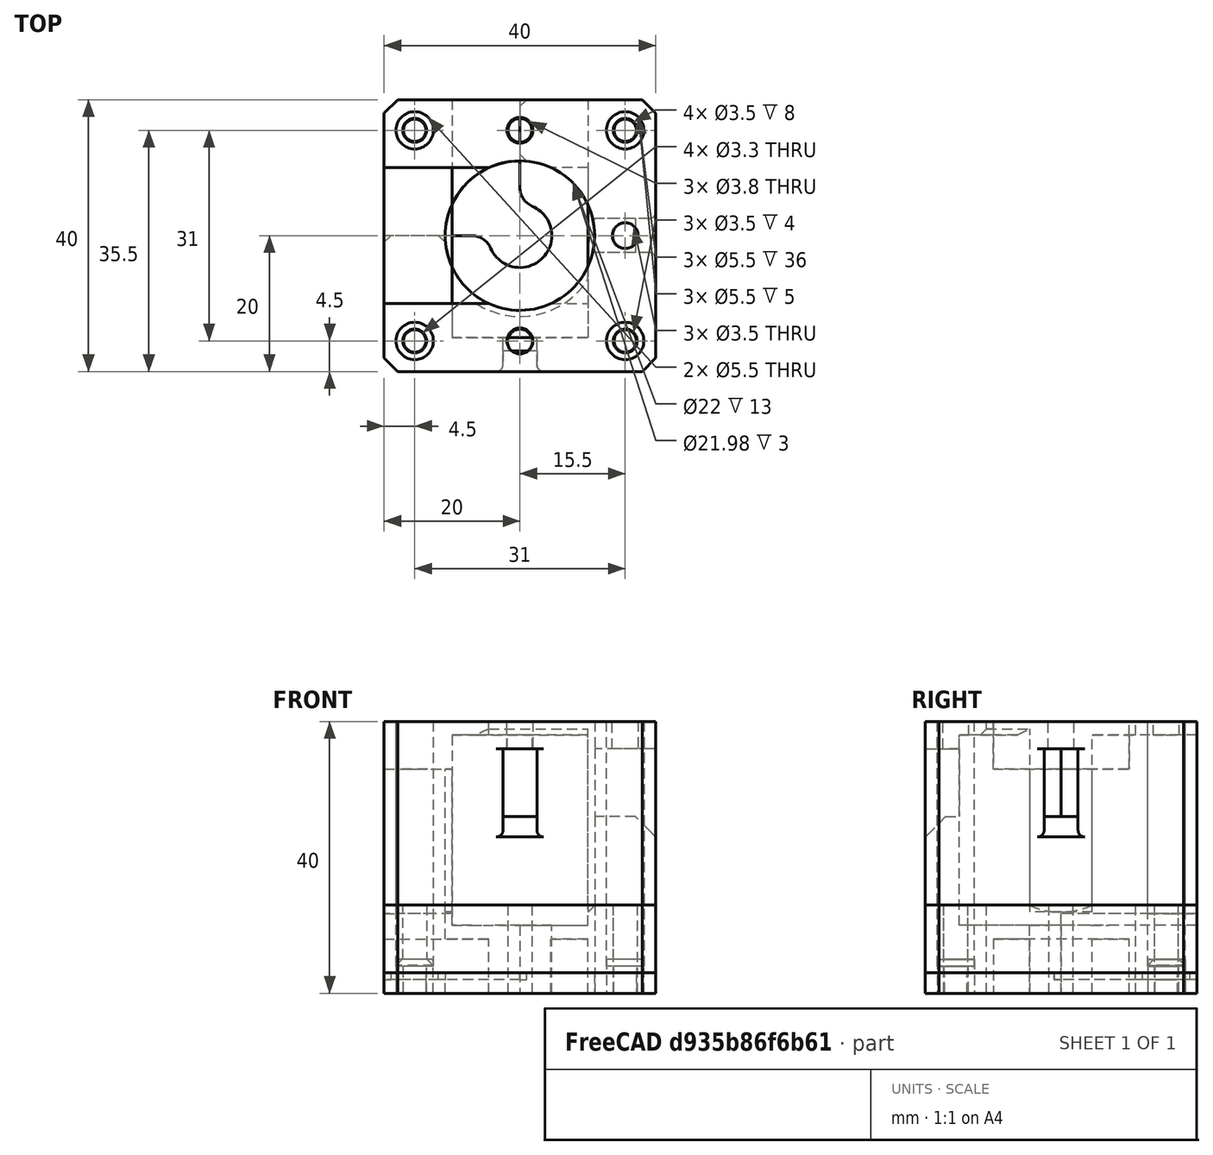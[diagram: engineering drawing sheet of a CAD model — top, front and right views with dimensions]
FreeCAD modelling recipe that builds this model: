
FCSTD DOCUMENT  (FreeCAD 0.19R)
Label: StepperTower
License: All rights reserved
LicenseURL: http://en.wikipedia.org/wiki/All_rights_reserved
objects: Sketcher::SketchObject×21, PartDesign::Pocket×17, PartDesign::Chamfer×7, PartDesign::Pad×3, PartDesign::Body×3, PartDesign::Fillet×2, Mesh::Feature×1
note: 82 computed .brp shape members not serialized (recipe doc carries the construction recipe); baked Part::Feature solids carry a one-line shape summary decoded from their .brp

FEATURE [Sketcher::SketchObject] Sketch  label="body"
  FullyConstrained = true
  MapMode = 5
  Support = -> [XY_Plane]
  sketch-geometry (4):
    g0: LineSegment StartX=-20 StartY=20 StartZ=0 EndX=20 EndY=20 EndZ=0
    g1: LineSegment StartX=20 StartY=20 StartZ=0 EndX=20 EndY=-20 EndZ=0
    g2: LineSegment StartX=20 StartY=-20 StartZ=0 EndX=-20 EndY=-20 EndZ=0
    g3: LineSegment StartX=-20 StartY=-20 StartZ=0 EndX=-20 EndY=20 EndZ=0
  constraints (11):
    c: Coincident(g0,g1)
    c: Coincident(g1,g2)
    c: Coincident(g2,g3)
    c: Coincident(g3,g0)
    c: Horizontal(g0)
    c: Horizontal(g2)
    c: Vertical(g1)
    c: Vertical(g3)
    c: Symmetric(g1,g0,g-1)
    c: Equal(g0,g1)
    c: Distance(g0) = 40
FEATURE [PartDesign::Pad] Pad
  Direction = (1,1,1)
  Length = 3
  Length2 = 100
  Profile = -> Sketch
  Type = 0
FEATURE [Sketcher::SketchObject] Sketch001  label="Holes"
  FullyConstrained = true
  MapMode = 5
  Placement = pos=(0,0,3) rot=(0,0,1;0rad)
  Support = -> [Pad]
  sketch-geometry (9):
    g0: Circle CenterX=0 CenterY=0 CenterZ=0 NormalX=0 NormalY=0 NormalZ=1 AngleXU=0 Radius=10.99
    g1: Circle CenterX=-15.5 CenterY=15.5 CenterZ=0 NormalX=0 NormalY=0 NormalZ=1 AngleXU=0 Radius=1.65
    g2: Circle CenterX=15.5 CenterY=15.5 CenterZ=0 NormalX=0 NormalY=0 NormalZ=1 AngleXU=0 Radius=1.65
    g3: Circle CenterX=-15.5 CenterY=-15.5 CenterZ=0 NormalX=0 NormalY=0 NormalZ=1 AngleXU=0 Radius=1.65
    g4: Circle CenterX=15.5 CenterY=-15.5 CenterZ=0 NormalX=0 NormalY=0 NormalZ=1 AngleXU=0 Radius=1.65
    g5: LineSegment StartX=-15.5 StartY=15.5 StartZ=0 EndX=15.5 EndY=15.5 EndZ=0
    g6: LineSegment StartX=15.5 StartY=15.5 StartZ=0 EndX=15.5 EndY=-15.5 EndZ=0
    g7: LineSegment StartX=15.5 StartY=-15.5 StartZ=0 EndX=-15.5 EndY=-15.5 EndZ=0
    g8: LineSegment StartX=-15.5 StartY=-15.5 StartZ=0 EndX=-15.5 EndY=15.5 EndZ=0
  constraints (21):
    c: Coincident(g0,g-1)
    c: Diameter(g0) = 21.98
    c: Coincident(g5,g1)
    c: Coincident(g5,g2)
    c: Horizontal(g5)
    c: Coincident(g5,g6)
    c: Coincident(g6,g4)
    c: Coincident(g6,g7)
    c: Coincident(g7,g3)
    c: Horizontal(g7)
    c: Coincident(g7,g8)
    c: Coincident(g8,g5)
    c: Vertical(g8)
    c: Equal(g5,g8)
    c: Equal(g8,g7)
    c: Symmetric(g2,g3,g0)
    c: Distance(g5) = 31
    c: Diameter(g2) = 3.3
    c: Equal(g2,g1)
    c: Equal(g2,g3)
    c: Equal(g2,g4)
FEATURE [PartDesign::Pocket] Pocket
  BaseFeature = -> Pad
  Length = 5
  Length2 = 100
  Profile = -> Sketch001
  Type = 0
FEATURE [Sketcher::SketchObject] Sketch002
  FullyConstrained = true
  MapMode = 5
  Placement = pos=(0,0,3) rot=(0,0,1;0rad)
  Support = -> [Pocket]
FEATURE [Sketcher::SketchObject] Sketch003
  FullyConstrained = false
  MapMode = 5
  Placement = pos=(0,0,3) rot=(0,0,1;0rad)
  Support = -> [Pocket]
  sketch-geometry (6):
    g0: Circle CenterX=0 CenterY=0 CenterZ=0 NormalX=0 NormalY=0 NormalZ=1 AngleXU=0 Radius=4.8
    g1: LineSegment StartX=-4.8 StartY=-1.92708e-05 StartZ=0 EndX=-4.8 EndY=45.1031 EndZ=0
    g2: LineSegment StartX=0 StartY=0 StartZ=0 EndX=-37.5429 EndY=0 EndZ=0
    g3: LineSegment StartX=-37.5429 StartY=0 StartZ=0 EndX=-37.5429 EndY=30.9278 EndZ=0
    g4: LineSegment StartX=-37.5429 StartY=30.9278 StartZ=0 EndX=0 EndY=30.9278 EndZ=0
    g5: LineSegment StartX=0 StartY=30.9278 StartZ=0 EndX=0 EndY=0 EndZ=0
  constraints (14):
    c: Coincident(g0,g-1)
    c: Diameter(g0) = 9.6
    c: PointOnObject(g1,g0)
    c: Vertical(g1)
    c: Tangent(g1,g0)
    c: Coincident(g2,g3)
    c: Coincident(g3,g4)
    c: Coincident(g4,g5)
    c: Coincident(g5,g2)
    c: Horizontal(g2)
    c: Horizontal(g4)
    c: Vertical(g3)
    c: Vertical(g5)
    c: Coincident(g2,g-1)
FEATURE [PartDesign::Pocket] Pocket001
  BaseFeature = -> Pocket
  Length = 1
  Length2 = 100
  Profile = -> Sketch003
  Type = 0
FEATURE [PartDesign::Chamfer] Chamfer
  Angle = 45
  Base = -> Pocket001 [Edge33,Edge15,Edge2,Edge6]
  BaseFeature = -> Pocket001
  ChamferType = 0
  FlipDirection = false
  Size = 2
  Size2 = 1
  SupportTransform = false
FEATURE [PartDesign::Chamfer] Chamfer001
  Angle = 45
  Base = -> Chamfer [Edge50,Edge6,Edge40,Edge42]
  BaseFeature = -> Chamfer
  ChamferType = 0
  FlipDirection = false
  Size = 1
  Size2 = 1
  SupportTransform = false
FEATURE [PartDesign::Body] Body  label="YSwasher"
  Group = -> [Sketch,Pad,Sketch001,Pocket,Sketch002,Sketch003,Pocket001,Chamfer,Chamfer001]
  Origin = -> Origin
  Tip = -> Chamfer001
FEATURE [Sketcher::SketchObject] Sketch004  label="Body002"
  FullyConstrained = true
  MapMode = 5
  Support = -> [XY_Plane001]
  sketch-geometry (4):
    g0: LineSegment StartX=-20 StartY=20 StartZ=0 EndX=20 EndY=20 EndZ=0
    g1: LineSegment StartX=20 StartY=20 StartZ=0 EndX=20 EndY=-20 EndZ=0
    g2: LineSegment StartX=20 StartY=-20 StartZ=0 EndX=-20 EndY=-20 EndZ=0
    g3: LineSegment StartX=-20 StartY=-20 StartZ=0 EndX=-20 EndY=20 EndZ=0
  constraints (11):
    c: Coincident(g0,g1)
    c: Coincident(g1,g2)
    c: Coincident(g2,g3)
    c: Coincident(g3,g0)
    c: Horizontal(g0)
    c: Horizontal(g2)
    c: Vertical(g1)
    c: Vertical(g3)
    c: Equal(g2,g3)
    c: Symmetric(g0,g2,g-1)
    c: Distance(g0) = 40
FEATURE [PartDesign::Pad] Pad001
  Direction = (1,1,1)
  Length = 40
  Length2 = 100
  Profile = -> Sketch004
  Type = 0
FEATURE [Sketcher::SketchObject] Sketch005  label="AluNotch"
  FullyConstrained = false
  MapMode = 5
  Placement = pos=(0,0,0) rot=(1,0,0;3.14159rad)
  Support = -> [Pad001]
  sketch-geometry (4):
    g0: LineSegment StartX=0 StartY=0 StartZ=0 EndX=-38.2164 EndY=0 EndZ=0
    g1: LineSegment StartX=-38.2164 StartY=0 StartZ=0 EndX=-38.2164 EndY=-40.583 EndZ=0
    g2: LineSegment StartX=-38.2164 StartY=-40.583 StartZ=0 EndX=0 EndY=-40.583 EndZ=0
    g3: LineSegment StartX=0 StartY=-40.583 StartZ=0 EndX=0 EndY=0 EndZ=0
  constraints (9):
    c: Coincident(g0,g1)
    c: Coincident(g1,g2)
    c: Coincident(g2,g3)
    c: Coincident(g3,g0)
    c: Horizontal(g0)
    c: Horizontal(g2)
    c: Vertical(g1)
    c: Vertical(g3)
    c: Coincident(g0,g-1)
FEATURE [PartDesign::Pocket] Pocket002
  BaseFeature = -> Pad001
  Length = 11.7
  Length2 = 100
  Profile = -> Sketch005
  Type = 0
FEATURE [Sketcher::SketchObject] Sketch006
  FullyConstrained = true
  MapMode = 5
  Placement = pos=(0,0,0) rot=(1,0,0;3.14159rad)
  Support = -> [Pocket002]
  sketch-geometry (8):
    g0: Circle CenterX=-15.5 CenterY=15.5 CenterZ=0 NormalX=0 NormalY=0 NormalZ=1 AngleXU=0 Radius=1.75
    g1: Circle CenterX=15.5 CenterY=15.5 CenterZ=0 NormalX=0 NormalY=0 NormalZ=1 AngleXU=0 Radius=1.75
    g2: Circle CenterX=-15.5 CenterY=-15.5 CenterZ=0 NormalX=0 NormalY=0 NormalZ=1 AngleXU=0 Radius=1.75
    g3: Circle CenterX=15.5 CenterY=-15.5 CenterZ=0 NormalX=0 NormalY=0 NormalZ=1 AngleXU=0 Radius=1.75
    g4: LineSegment StartX=-15.5 StartY=15.5 StartZ=0 EndX=15.5 EndY=15.5 EndZ=0
    g5: LineSegment StartX=15.5 StartY=15.5 StartZ=0 EndX=15.5 EndY=-15.5 EndZ=0
    g6: LineSegment StartX=15.5 StartY=-15.5 StartZ=0 EndX=-15.5 EndY=-15.5 EndZ=0
    g7: LineSegment StartX=-15.5 StartY=-15.5 StartZ=0 EndX=-15.5 EndY=15.5 EndZ=0
  constraints (19):
    c: Coincident(g4,g0)
    c: Coincident(g4,g1)
    c: Horizontal(g4)
    c: Coincident(g4,g5)
    c: Coincident(g5,g3)
    c: Vertical(g5)
    c: Coincident(g5,g6)
    c: Coincident(g6,g2)
    c: Coincident(g6,g7)
    c: Coincident(g7,g4)
    c: Vertical(g7)
    c: Equal(g7,g4)
    c: Equal(g4,g5)
    c: Symmetric(g1,g2,g-1)
    c: Diameter(g0) = 3.5
    c: Equal(g0,g1)
    c: Equal(g0,g3)
    c: Equal(g0,g2)
    c: Distance(g4) = 31
FEATURE [PartDesign::Pocket] Pocket003
  BaseFeature = -> Pocket002
  Length = 5
  Length2 = 100
  Profile = -> Sketch006
  Type = 1
FEATURE [Sketcher::SketchObject] Sketch007  label="pulleyDoor"
  FullyConstrained = true
  MapMode = 5
  Placement = pos=(0,20,0) rot=(0,0.707107,0.707107;3.14159rad)
  Support = -> [Pocket003]
  sketch-geometry (4):
    g0: LineSegment StartX=-10 StartY=38 StartZ=0 EndX=10 EndY=38 EndZ=0
    g1: LineSegment StartX=10 StartY=38 StartZ=0 EndX=10 EndY=10 EndZ=0
    g2: LineSegment StartX=10 StartY=10 StartZ=0 EndX=-10 EndY=10 EndZ=0
    g3: LineSegment StartX=-10 StartY=10 StartZ=0 EndX=-10 EndY=38 EndZ=0
  constraints (11):
    c: Coincident(g0,g1)
    c: Coincident(g1,g2)
    c: Coincident(g2,g3)
    c: Coincident(g3,g0)
    c: Horizontal(g0)
    c: Vertical(g1)
    c: Vertical(g3)
    c: Symmetric(g1,g2,g-2)
    c: Distance(g2) = 20
    c: DistanceY(g1,g1) = 28
    c: DistanceY(g1) = 10
FEATURE [PartDesign::Pocket] Pocket004
  BaseFeature = -> Pocket003
  Length = 35
  Length2 = 100
  Profile = -> Sketch007
  Type = 0
FEATURE [Sketcher::SketchObject] Sketch009  label="stepperRingHol"
  FullyConstrained = true
  MapMode = 5
  Placement = pos=(0,0,40) rot=(0,0,1;0rad)
  Support = -> [Pocket004]
  sketch-geometry (1):
    g0: Circle CenterX=0 CenterY=0 CenterZ=0 NormalX=0 NormalY=0 NormalZ=1 AngleXU=0 Radius=11
  constraints (2):
    c: Coincident(g0,g-1)
    c: Diameter(g0) = 22
FEATURE [PartDesign::Pocket] Pocket005
  BaseFeature = -> Pocket004
  Length = 28
  Length2 = 100
  Profile = -> Sketch009
  Type = 0
FEATURE [Sketcher::SketchObject] Sketch011  label="countersink"
  FullyConstrained = true
  MapMode = 5
  Placement = pos=(0,0,40) rot=(0,0,1;0rad)
  Support = -> [Pocket005]
  sketch-geometry (8):
    g0: Circle CenterX=-15.5 CenterY=-15.5 CenterZ=0 NormalX=0 NormalY=0 NormalZ=1 AngleXU=0 Radius=2.75
    g1: Circle CenterX=-15.5 CenterY=15.5 CenterZ=0 NormalX=0 NormalY=0 NormalZ=1 AngleXU=0 Radius=2.75
    g2: Circle CenterX=15.5 CenterY=15.5 CenterZ=0 NormalX=0 NormalY=0 NormalZ=1 AngleXU=0 Radius=2.75
    g3: Circle CenterX=15.5 CenterY=-15.5 CenterZ=0 NormalX=0 NormalY=0 NormalZ=1 AngleXU=0 Radius=2.75
    g4: LineSegment StartX=-15.5 StartY=15.5 StartZ=0 EndX=15.5 EndY=15.5 EndZ=0
    g5: LineSegment StartX=15.5 StartY=15.5 StartZ=0 EndX=15.5 EndY=-15.5 EndZ=0
    g6: LineSegment StartX=15.5 StartY=-15.5 StartZ=0 EndX=-15.5 EndY=-15.5 EndZ=0
    g7: LineSegment StartX=-15.5 StartY=-15.5 StartZ=0 EndX=-15.5 EndY=15.5 EndZ=0
  constraints (19):
    c: Diameter(g0) = 5.5
    c: Coincident(g4,g1)
    c: Coincident(g4,g2)
    c: Horizontal(g4)
    c: Coincident(g4,g5)
    c: Coincident(g5,g3)
    c: Vertical(g5)
    c: Coincident(g5,g6)
    c: Coincident(g6,g0)
    c: Horizontal(g6)
    c: Coincident(g6,g7)
    c: Coincident(g7,g4)
    c: Vertical(g7)
    c: Equal(g4,g7)
    c: Symmetric(g1,g3,g-1)
    c: Distance(g4) = 31
    c: Diameter(g1) = 5.5
    c: Equal(g1,g2)
    c: Equal(g1,g3)
FEATURE [PartDesign::Pocket] Pocket006
  BaseFeature = -> Pocket005
  Length = 36
  Length2 = 100
  Profile = -> Sketch011
  Type = 0
FEATURE [Sketcher::SketchObject] Sketch012
  FullyConstrained = true
  MapMode = 5
  Placement = pos=(0,0,40) rot=(0,0,1;0rad)
  Support = -> [Pocket006]
  sketch-geometry (4):
    g0: Circle CenterX=0 CenterY=15.5 CenterZ=0 NormalX=0 NormalY=0 NormalZ=1 AngleXU=0 Radius=1.9
    g1: Circle CenterX=15.5 CenterY=0 CenterZ=0 NormalX=0 NormalY=0 NormalZ=1 AngleXU=0 Radius=1.9
    g2: Circle CenterX=0 CenterY=-15.5 CenterZ=0 NormalX=0 NormalY=0 NormalZ=1 AngleXU=0 Radius=1.9
    g3: Circle CenterX=-15.5 CenterY=0 CenterZ=0 NormalX=0 NormalY=0 NormalZ=1 AngleXU=0 Radius=1.9
  constraints (10):
    c: PointOnObject(g0,g-2)
    c: PointOnObject(g1,g-1)
    c: Diameter(g3) = 3.8
    c: Equal(g3,g0)
    c: Equal(g3,g1)
    c: Equal(g3,g2)
    c: Symmetric(g2,g0,g-1)
    c: Distance(g0,g2) = 31
    c: Distance(g1,g3) = 31
    c: Symmetric(g1,g3,g-1)
FEATURE [PartDesign::Pocket] Pocket007
  BaseFeature = -> Pocket006
  Length = 7
  Length2 = 100
  Profile = -> Sketch012
  Type = 0
FEATURE [Sketcher::SketchObject] Sketch013
  FullyConstrained = true
  MapMode = 5
  Support = -> [XY_Plane002]
  sketch-geometry (4):
    g0: LineSegment StartX=-20 StartY=20 StartZ=0 EndX=20 EndY=20 EndZ=0
    g1: LineSegment StartX=20 StartY=20 StartZ=0 EndX=20 EndY=-20 EndZ=0
    g2: LineSegment StartX=20 StartY=-20 StartZ=0 EndX=-20 EndY=-20 EndZ=0
    g3: LineSegment StartX=-20 StartY=-20 StartZ=0 EndX=-20 EndY=20 EndZ=0
  constraints (11):
    c: Coincident(g0,g1)
    c: Coincident(g1,g2)
    c: Coincident(g2,g3)
    c: Coincident(g3,g0)
    c: Horizontal(g0)
    c: Horizontal(g2)
    c: Vertical(g1)
    c: Vertical(g3)
    c: Distance(g2) = 40
    c: Equal(g1,g2)
    c: Symmetric(g1,g0,g-1)
FEATURE [PartDesign::Pad] Pad002
  Direction = (1,1,1)
  Length = 13
  Length2 = 100
  Profile = -> Sketch013
  Type = 0
FEATURE [Sketcher::SketchObject] Sketch014
  FullyConstrained = false
  MapMode = 5
  Placement = pos=(-20,0,0) rot=(0.57735,-0.57735,-0.57735;2.0944rad)
  Support = -> [Pad002]
  sketch-geometry (4):
    g0: LineSegment StartX=-10 StartY=8 StartZ=0 EndX=10 EndY=8 EndZ=0
    g1: LineSegment StartX=10 StartY=8 StartZ=0 EndX=10 EndY=-11.7865 EndZ=0
    g2: LineSegment StartX=10 StartY=-11.7865 StartZ=0 EndX=-10 EndY=-11.7865 EndZ=0
    g3: LineSegment StartX=-10 StartY=-11.7865 StartZ=0 EndX=-10 EndY=8 EndZ=0
  constraints (10):
    c: Coincident(g0,g1)
    c: Coincident(g1,g2)
    c: Coincident(g2,g3)
    c: Coincident(g3,g0)
    c: Horizontal(g2)
    c: Vertical(g1)
    c: Vertical(g3)
    c: Distance(g0) = 20
    c: Symmetric(g0,g0,g-2)
    c: DistanceY(g0) = 8
FEATURE [PartDesign::Pocket] Pocket008
  BaseFeature = -> Pad002
  Length = 30
  Length2 = 100
  Profile = -> Sketch014
  Type = 0
FEATURE [Sketcher::SketchObject] Sketch015
  FullyConstrained = true
  MapMode = 5
  Placement = pos=(0,0,13) rot=(0,0,1;0rad)
  Support = -> [Pocket008]
  sketch-geometry (1):
    g0: Circle CenterX=0 CenterY=0 CenterZ=0 NormalX=0 NormalY=0 NormalZ=1 AngleXU=0 Radius=11
  constraints (2):
    c: Coincident(g0,g-1)
    c: Diameter(g0) = 22
FEATURE [PartDesign::Pocket] Pocket009
  BaseFeature = -> Pocket008
  Length = 2
  Length2 = 100
  Profile = -> Sketch015
  Type = 1
FEATURE [Sketcher::SketchObject] Sketch017
  FullyConstrained = true
  MapMode = 5
  Placement = pos=(0,0,13) rot=(0,0,1;0rad)
  Support = -> [Pocket009]
  sketch-geometry (7):
    g0: Circle CenterX=0 CenterY=15.5 CenterZ=0 NormalX=0 NormalY=0 NormalZ=1 AngleXU=0 Radius=1.75
    g1: Circle CenterX=15.5 CenterY=0 CenterZ=0 NormalX=0 NormalY=0 NormalZ=1 AngleXU=0 Radius=1.75
    g2: Circle CenterX=0 CenterY=-15.5 CenterZ=0 NormalX=0 NormalY=0 NormalZ=1 AngleXU=0 Radius=1.75
    g3: Circle CenterX=-15.5 CenterY=15.5 CenterZ=0 NormalX=0 NormalY=0 NormalZ=1 AngleXU=0 Radius=1.75
    g4: Circle CenterX=15.5 CenterY=15.5 CenterZ=0 NormalX=0 NormalY=0 NormalZ=1 AngleXU=0 Radius=1.75
    g5: Circle CenterX=-15.5 CenterY=-15.5 CenterZ=0 NormalX=0 NormalY=0 NormalZ=1 AngleXU=0 Radius=1.75
    g6: Circle CenterX=15.5 CenterY=-15.5 CenterZ=0 NormalX=0 NormalY=0 NormalZ=1 AngleXU=0 Radius=1.75
  constraints (17):
    c: PointOnObject(g0,g-2)
    c: PointOnObject(g1,g-1)
    c: Distance(g0,g2) = 31
    c: Symmetric(g2,g0,g-1)
    c: DistanceX(g1) = 15.5
    c: Diameter(g2) = 3.5
    c: Equal(g2,g1)
    c: Equal(g2,g0)
    c: Symmetric(g6,g3,g-1)
    c: Symmetric(g4,g6,g-1)
    c: Symmetric(g5,g3,g-1)
    c: Distance(g4,g3) = 31
    c: Diameter(g4) = 3.5
    c: Equal(g4,g3)
    c: Equal(g4,g6)
    c: Equal(g4,g5)
    c: Distance(g3,g5) = 31
FEATURE [Sketcher::SketchObject] Sketch018
  FullyConstrained = true
  MapMode = 5
  Placement = pos=(0,0,20) rot=(0,0,1;0rad)
  sketch-geometry (3):
    g0: Circle CenterX=0 CenterY=15.5 CenterZ=0 NormalX=0 NormalY=0 NormalZ=1 AngleXU=0 Radius=1.9
    g1: Circle CenterX=15.5 CenterY=0 CenterZ=0 NormalX=0 NormalY=0 NormalZ=1 AngleXU=0 Radius=1.9
    g2: Circle CenterX=0 CenterY=-15.5 CenterZ=0 NormalX=0 NormalY=0 NormalZ=1 AngleXU=0 Radius=1.9
  constraints (9):
    c: PointOnObject(g0,g-2)
    c: PointOnObject(g1,g-1)
    c: PointOnObject(g2,g-2)
    c: DistanceY(g0) = 15.5
    c: DistanceY(g2) = -15.5
    c: DistanceX(g1) = 15.5
    c: Diameter(g0) = 3.8
    c: Equal(g0,g1)
    c: Equal(g0,g2)
FEATURE [Sketcher::SketchObject] Sketch019
  FullyConstrained = true
  MapMode = 5
  Placement = pos=(0,0,0) rot=(1,0,0;3.14159rad)
  sketch-geometry (8):
    g0: Circle CenterX=-15.5 CenterY=15.5 CenterZ=0 NormalX=0 NormalY=0 NormalZ=1 AngleXU=0 Radius=2.75
    g1: Circle CenterX=15.5 CenterY=15.5 CenterZ=0 NormalX=0 NormalY=0 NormalZ=1 AngleXU=0 Radius=2.75
    g2: Circle CenterX=15.5 CenterY=-15.5 CenterZ=0 NormalX=0 NormalY=0 NormalZ=1 AngleXU=0 Radius=2.75
    g3: Circle CenterX=-15.5 CenterY=-15.5 CenterZ=0 NormalX=0 NormalY=0 NormalZ=1 AngleXU=0 Radius=2.75
    g4: LineSegment StartX=-15.5 StartY=15.5 StartZ=0 EndX=15.5 EndY=15.5 EndZ=0
    g5: LineSegment StartX=15.5 StartY=15.5 StartZ=0 EndX=15.5 EndY=-15.5 EndZ=0
    g6: LineSegment StartX=15.5 StartY=-15.5 StartZ=0 EndX=-15.5 EndY=-15.5 EndZ=0
    g7: LineSegment StartX=-15.5 StartY=-15.5 StartZ=0 EndX=-15.5 EndY=15.5 EndZ=0
  constraints (19):
    c: Diameter(g3) = 5.5
    c: Equal(g3,g0)
    c: Equal(g3,g1)
    c: Equal(g3,g2)
    c: Coincident(g4,g0)
    c: Coincident(g4,g1)
    c: Horizontal(g4)
    c: Coincident(g4,g5)
    c: Coincident(g5,g2)
    c: Vertical(g5)
    c: Coincident(g5,g6)
    c: Coincident(g6,g3)
    c: Horizontal(g6)
    c: Coincident(g6,g7)
    c: Coincident(g7,g4)
    c: Vertical(g7)
    c: Equal(g4,g5)
    c: Distance(g4) = 31
    c: Symmetric(g1,g3,g-1)
FEATURE [PartDesign::Pocket] Pocket010
  BaseFeature = -> Pocket009
  Length = 5
  Length2 = 100
  Profile = -> Sketch017
  Type = 1
FEATURE [PartDesign::Pocket] Pocket011
  BaseFeature = -> Pocket010
  Length = 5
  Length2 = 100
  Profile = -> Sketch018
  Type = 0
FEATURE [PartDesign::Pocket] Pocket012
  BaseFeature = -> Pocket011
  Length = 5
  Length2 = 100
  Profile = -> Sketch019
  Type = 0
FEATURE [PartDesign::Chamfer] Chamfer002
  Angle = 45
  Base = -> Pocket012 [Edge62,Edge70,Edge66]
  BaseFeature = -> Pocket012
  ChamferType = 0
  FlipDirection = false
  Size = 0.9
  Size2 = 1
  SupportTransform = false
FEATURE [PartDesign::Chamfer] Chamfer003
  Angle = 45
  Base = -> Pocket007 [Edge69,Edge65,Edge67]
  BaseFeature = -> Pocket007
  ChamferType = 0
  FlipDirection = false
  Size = 0.9
  Size2 = 1
  SupportTransform = false
FEATURE [PartDesign::Chamfer] Chamfer005
  Angle = 45
  Base = -> Chamfer002 [Edge43,Edge48,Edge51,Edge45]
  BaseFeature = -> Chamfer002
  ChamferType = 0
  FlipDirection = false
  Size = 2
  Size2 = 1
  SupportTransform = false
FEATURE [PartDesign::Body] Body002  label="XSblock"
  Group = -> [Sketch013,Pad002,Sketch014,Pocket008,Sketch015,Pocket009,Sketch017,Sketch018,Sketch019,Pocket010,Pocket011,Pocket012,Chamfer002,Chamfer005]
  Origin = -> Origin002
  Tip = -> Chamfer005
FEATURE [Sketcher::SketchObject] Sketch020
  FullyConstrained = false
  MapMode = 5
  Placement = pos=(0,0,0) rot=(1,0,0;3.14159rad)
  Support = -> [Chamfer003]
  sketch-geometry (1):
    g0: Circle CenterX=0 CenterY=0 CenterZ=0 NormalX=0 NormalY=0 NormalZ=1 AngleXU=0 Radius=4.69229
  constraints (1):
    c: Coincident(g0,g-1)
FEATURE [PartDesign::Pocket] Pocket013
  BaseFeature = -> Chamfer003
  Length = 5
  Length2 = 100
  Profile = -> Sketch020
  Type = 1
FEATURE [PartDesign::Fillet] Fillet
  Base = -> Pocket013 [Edge43,Edge78]
  BaseFeature = -> Pocket013
  Radius = 3
  SupportTransform = false
FEATURE [Sketcher::SketchObject] Sketch021
  FullyConstrained = true
  MapMode = 5
  Placement = pos=(20,0,0) rot=(0.57735,0.57735,0.57735;2.0944rad)
  Support = -> [Fillet]
  sketch-geometry (4):
    g0: LineSegment StartX=-2.5 StartY=36 StartZ=0 EndX=2.5 EndY=36 EndZ=0
    g1: LineSegment StartX=2.5 StartY=36 StartZ=0 EndX=2.5 EndY=26 EndZ=0
    g2: LineSegment StartX=2.5 StartY=26 StartZ=0 EndX=-2.5 EndY=26 EndZ=0
    g3: LineSegment StartX=-2.5 StartY=26 StartZ=0 EndX=-2.5 EndY=36 EndZ=0
  constraints (11):
    c: Coincident(g0,g1)
    c: Coincident(g1,g2)
    c: Coincident(g2,g3)
    c: Coincident(g3,g0)
    c: Horizontal(g0)
    c: Vertical(g1)
    c: Vertical(g3)
    c: Distance(g1) = 10
    c: Distance(g0) = 5
    c: Symmetric(g1,g2,g-2)
    c: DistanceY(g0) = 36
FEATURE [Sketcher::SketchObject] Sketch022
  FullyConstrained = true
  MapMode = 5
  Placement = pos=(0,-20,0) rot=(1,0,0;1.5708rad)
  sketch-geometry (4):
    g0: LineSegment StartX=-2.5 StartY=36 StartZ=0 EndX=2.5 EndY=36 EndZ=0
    g1: LineSegment StartX=2.5 StartY=36 StartZ=0 EndX=2.5 EndY=26 EndZ=0
    g2: LineSegment StartX=2.5 StartY=26 StartZ=0 EndX=-2.5 EndY=26 EndZ=0
    g3: LineSegment StartX=-2.5 StartY=26 StartZ=0 EndX=-2.5 EndY=36 EndZ=0
  constraints (11):
    c: Coincident(g0,g1)
    c: Coincident(g1,g2)
    c: Coincident(g2,g3)
    c: Coincident(g3,g0)
    c: Horizontal(g2)
    c: Vertical(g1)
    c: Vertical(g3)
    c: Symmetric(g0,g0,g-2)
    c: Distance(g0) = 5
    c: DistanceY(g0) = 36
    c: Distance(g1) = 10
FEATURE [PartDesign::Pocket] Pocket014
  BaseFeature = -> Fillet
  Length = 9
  Length2 = 100
  Profile = -> Sketch021
  Type = 0
FEATURE [PartDesign::Pocket] Pocket015
  BaseFeature = -> Pocket014
  Length = 12
  Length2 = 100
  Profile = -> Sketch022
  Type = 0
FEATURE [Sketcher::SketchObject] Sketch023
  FullyConstrained = false
  MapMode = 5
  Placement = pos=(-20,0,0) rot=(0.57735,-0.57735,-0.57735;2.0944rad)
  Support = -> [Pocket015]
  sketch-geometry (4):
    g0: LineSegment StartX=-10 StartY=47.4954 StartZ=0 EndX=10 EndY=47.4954 EndZ=0
    g1: LineSegment StartX=10 StartY=47.4954 StartZ=0 EndX=10 EndY=33 EndZ=0
    g2: LineSegment StartX=10 StartY=33 StartZ=0 EndX=-10 EndY=33 EndZ=0
    g3: LineSegment StartX=-10 StartY=33 StartZ=0 EndX=-10 EndY=47.4954 EndZ=0
  constraints (10):
    c: Coincident(g0,g1)
    c: Coincident(g1,g2)
    c: Coincident(g2,g3)
    c: Coincident(g3,g0)
    c: Horizontal(g0)
    c: Vertical(g1)
    c: Vertical(g3)
    c: DistanceY(g1) = 33
    c: Distance(g0) = 20
    c: Symmetric(g1,g2,g-2)
FEATURE [PartDesign::Pocket] Pocket016
  BaseFeature = -> Pocket015
  Length = 20
  Length2 = 100
  Profile = -> Sketch023
  Type = 0
FEATURE [PartDesign::Chamfer] Chamfer006
  Angle = 45
  Base = -> Pocket016 [Edge103,Edge109]
  BaseFeature = -> Pocket016
  ChamferType = 0
  FlipDirection = false
  Size = 3
  Size2 = 1
  SupportTransform = false
FEATURE [PartDesign::Chamfer] Chamfer007
  Angle = 45
  Base = -> Chamfer006 [Edge28,Edge103,Edge25,Edge74]
  BaseFeature = -> Chamfer006
  ChamferType = 0
  FlipDirection = false
  Size = 2
  Size2 = 1
  SupportTransform = false
FEATURE [PartDesign::Fillet] Fillet001
  Base = -> Chamfer007 [Edge10,Edge6,Edge76,Edge72]
  BaseFeature = -> Chamfer007
  Radius = 1
  SupportTransform = false
FEATURE [PartDesign::Body] Body001  label="YSBlock"
  Group = -> [Sketch004,Pad001,Sketch005,Pocket002,Sketch006,Pocket003,Sketch007,Pocket004,Sketch009,Sketch011,Pocket005,Pocket006,Sketch012,Pocket007,Chamfer003,Sketch020,Pocket013,Fillet,Sketch021,Sketch022,Pocket014,Pocket015,Sketch023,Pocket016,Chamfer006,Chamfer007,Fillet001]
  Origin = -> Origin001
  Tip = -> Fillet001
FEATURE [Mesh::Feature] Mesh  label="Chamfer005 (Meshed)"
